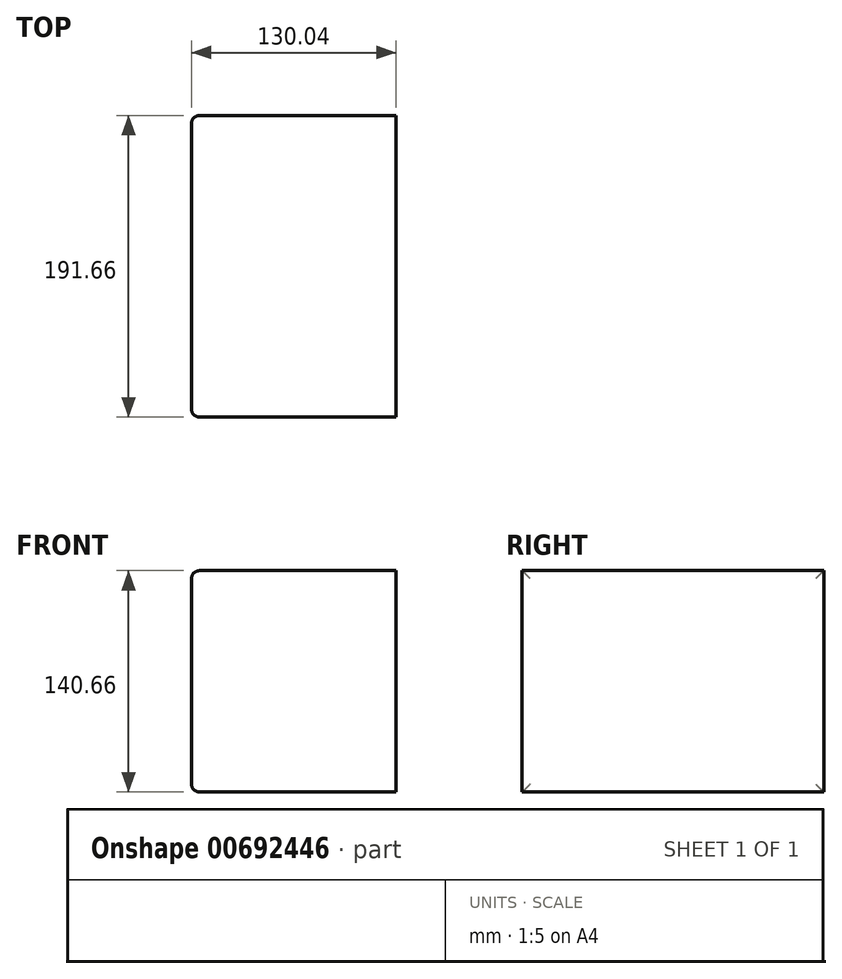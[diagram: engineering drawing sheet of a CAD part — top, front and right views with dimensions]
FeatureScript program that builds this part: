
annotation { "Feature Type Name" : "Feature", "Feature Type Description" : "" }
export const myFeature = defineFeature(function(context is Context, id is Id, definition is map)
    precondition{}
    {
        {
            var Q0;
            Q0=qCreatedBy(makeId("Top.planeOp"),FACE);
            var sketch = newSketch(context, id + "F0", { "sketchPlane" : qUnion([Q0])});
            skLineSegment(sketch, "E0.bottom", {"start": v(-49.96, 42.02) * mm, "end": v(80.08, 42.02) * mm});
            skLineSegment(sketch, "E0.top", {"start": v(-49.96, -149.64) * mm, "end": v(80.08, -149.64) * mm});
            skLineSegment(sketch, "E0.left", {"start": v(-49.96, 42.02) * mm, "end": v(-49.96, -149.64) * mm});
            skLineSegment(sketch, "E0.right", {"start": v(80.08, 42.02) * mm, "end": v(80.08, -149.64) * mm});
            skSolve(sketch);
        }
        {
            var Q0;
            Q0 = qSketchRegion(id + "F0", true);
            extrude(context, id + "F1", {"entities" : qUnion([Q0]), "depth" : 140.66 * mm, "offsetDistance" : 25.4 * mm});
        }
        {
            var Q0;
            Q0=makeQuery(id+"F1.opExtrude","CAP_EDGE",EDGE,{"disambiguationData":[OSD([sQuery(id+"F0.wireOp",EDGE,"E0.left")])],"isStart":true});
            var Q1;
            Q1=makeQuery(id+"F1.opExtrude","SWEPT_FACE",FACE,{"disambiguationData":[OSD([sQuery(id+"F0.wireOp",EDGE,"E0.left")])]});
            fillet(context, id + "F2", {"entities" : qUnion([Q0, Q1]), "radius" : 5.08 * mm, "tangentPropagation" : true, "allowEdgeOverflow" : false});
        }
    });
